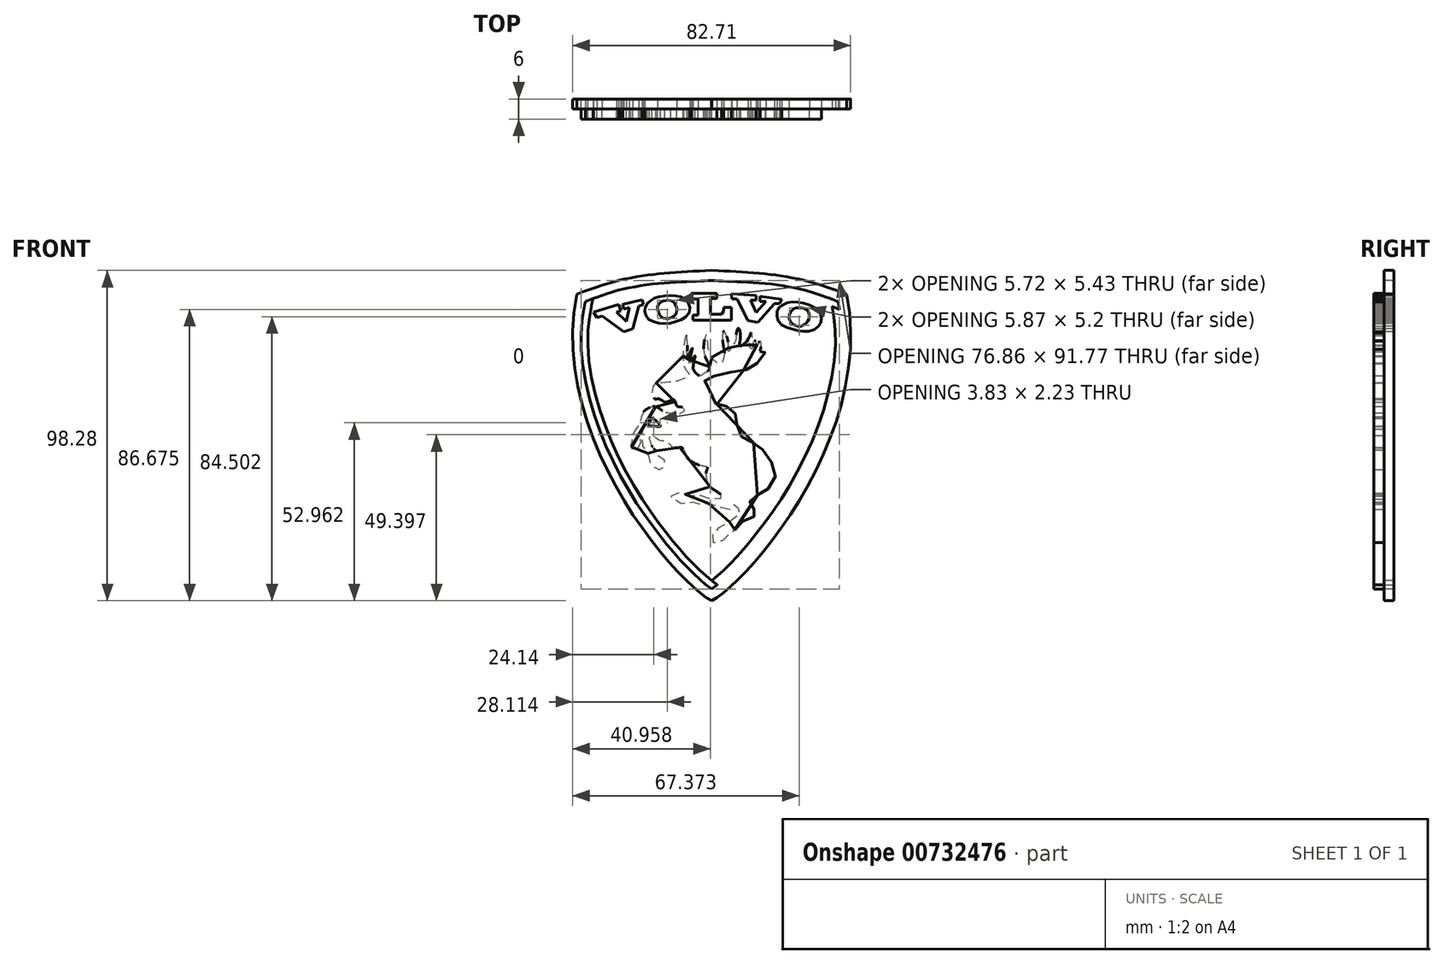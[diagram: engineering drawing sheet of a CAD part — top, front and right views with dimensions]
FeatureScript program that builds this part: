
annotation { "Feature Type Name" : "Feature", "Feature Type Description" : "" }
export const myFeature = defineFeature(function(context is Context, id is Id, definition is map)
    precondition{}
    {
        {
            var Q0;
            Q0=qCreatedBy(makeId("Front.planeOp"),FACE);
            var sketch = newSketch(context, id + "F0", { "sketchPlane" : qUnion([Q0])});
            skFitSpline(sketch, "E0", {"points": [v(28.32, -35.45) * mm, v(-11.84, 55.74) * mm], "startDerivative": vector(-32.94, 17.67) * mm, "endDerivative": vector(24.9, 126.93) * mm});
            skFitSpline(sketch, "E1", {"points": [v(-11.84, 55.74) * mm, v(28.32, 62.83) * mm], "startDerivative": vector(45.8, 18.48) * mm, "endDerivative": vector(43.78, 2) * mm});
            skFitSpline(sketch, "E2.MirrorCS", {"points": [v(68.5, 55.74) * mm, v(28.32, 62.83) * mm], "startDerivative": vector(-45.8, 18.48) * mm, "endDerivative": vector(-43.78, 2) * mm});
            skFitSpline(sketch, "E3.MirrorCS", {"points": [v(28.32, -35.45) * mm, v(68.5, 55.74) * mm], "startDerivative": vector(32.94, 17.67) * mm, "endDerivative": vector(-24.9, 126.93) * mm});
            skFitSpline(sketch, "E4.0", {"points": [v(29.74, -32.8) * mm, v(29.49, -32.67) * mm, v(28.89, -32.31) * mm, v(27.42, -31.29) * mm, v(25.17, -29.46) * mm, v(22.01, -26.47) * mm, v(18.52, -22.77) * mm, v(14.82, -18.42) * mm, v(9.76, -11.84) * mm, v(3.46, -2.28) * mm, v(-3.2, 10.82) * mm, v(-8.13, 25.08) * mm, v(-10.5, 40.02) * mm, v(-9.89, 50.13) * mm, v(-8.9, 55.16) * mm]});
            skFitSpline(sketch, "E4.1", {"points": [v(26.9, -32.8) * mm, v(27.16, -32.67) * mm, v(27.76, -32.31) * mm, v(29.23, -31.29) * mm, v(31.48, -29.46) * mm, v(34.64, -26.47) * mm, v(38.13, -22.77) * mm, v(41.83, -18.42) * mm, v(46.9, -11.84) * mm, v(53.2, -2.28) * mm, v(59.85, 10.82) * mm, v(64.78, 25.08) * mm, v(67.16, 40.02) * mm, v(66.54, 50.13) * mm, v(65.55, 55.16) * mm]});
            skFitSpline(sketch, "E4.2", {"points": [v(67.37, 52.95) * mm, v(63.66, 54.45) * mm, v(56.88, 56.72) * mm, v(47.72, 58.54) * mm, v(38.57, 59.38) * mm, v(31.84, 59.67) * mm, v(28.19, 59.84) * mm]});
            skFitSpline(sketch, "E4.3", {"points": [v(-10.72, 52.95) * mm, v(-7, 54.45) * mm, v(-0.23, 56.72) * mm, v(8.92, 58.54) * mm, v(18.08, 59.38) * mm, v(24.8, 59.67) * mm, v(28.46, 59.84) * mm]});
            skFitSpline(sketch, "E5.0", {"points": [v(30.69, -31.04) * mm, v(30.5, -30.94) * mm, v(29.99, -30.64) * mm, v(28.64, -29.7) * mm, v(26.5, -27.96) * mm, v(23.43, -25.06) * mm, v(20.01, -21.44) * mm, v(16.38, -17.17) * mm, v(11.4, -10.68) * mm, v(5.19, -1.27) * mm, v(-1.36, 11.61) * mm, v(-6.18, 25.59) * mm, v(-8.5, 40.13) * mm, v(-7.9, 49.91) * mm, v(-6.94, 54.77) * mm]});
            skFitSpline(sketch, "E5.1", {"points": [v(25.96, -31.04) * mm, v(26.15, -30.94) * mm, v(26.66, -30.64) * mm, v(28, -29.7) * mm, v(30.15, -27.96) * mm, v(33.22, -25.06) * mm, v(36.63, -21.44) * mm, v(40.27, -17.17) * mm, v(45.25, -10.68) * mm, v(51.46, -1.27) * mm, v(58, 11.61) * mm, v(62.83, 25.59) * mm, v(65.14, 40.13) * mm, v(64.54, 49.91) * mm, v(63.59, 54.77) * mm]});
            skFitSpline(sketch, "E5.2", {"points": [v(66.62, 51.1) * mm, v(62.98, 52.57) * mm, v(56.36, 54.78) * mm, v(47.45, 56.55) * mm, v(38.46, 57.39) * mm, v(31.76, 57.67) * mm, v(28.1, 57.84) * mm]});
            skFitSpline(sketch, "E5.3", {"points": [v(-9.97, 51.1) * mm, v(-6.33, 52.57) * mm, v(0.3, 54.78) * mm, v(9.2, 56.55) * mm, v(18.2, 57.39) * mm, v(24.9, 57.67) * mm, v(28.55, 57.84) * mm]});
            skLineSegment(sketch, "E6", {"start": v(-5.84, 48.83) * mm, "end": v(-4.27, 49.28) * mm});
            skLineSegment(sketch, "E7", {"start": v(-4.27, 49.28) * mm, "end": v(2.15, 44.6) * mm});
            skLineSegment(sketch, "E8", {"start": v(2.15, 44.6) * mm, "end": v(4.85, 45.45) * mm});
            skLineSegment(sketch, "E9", {"start": v(4.85, 45.45) * mm, "end": v(6.6, 52.26) * mm});
            skLineSegment(sketch, "E10", {"start": v(6.6, 52.26) * mm, "end": v(8.06, 52.71) * mm});
            skLineSegment(sketch, "E11", {"start": v(8.06, 52.71) * mm, "end": v(7.63, 54.12) * mm});
            skLineSegment(sketch, "E12", {"start": v(7.63, 54.12) * mm, "end": v(1.81, 52.71) * mm});
            skLineSegment(sketch, "E13", {"start": v(1.81, 52.71) * mm, "end": v(2.25, 51.3) * mm});
            skLineSegment(sketch, "E14", {"start": v(2.25, 51.3) * mm, "end": v(3.82, 51.79) * mm});
            skLineSegment(sketch, "E15", {"start": v(3.82, 51.79) * mm, "end": v(2.94, 47.7) * mm});
            skLineSegment(sketch, "E16", {"start": v(2.94, 47.7) * mm, "end": v(0, 50.4) * mm});
            skLineSegment(sketch, "E17", {"start": v(0, 50.4) * mm, "end": v(1.25, 50.79) * mm});
            skLineSegment(sketch, "E18", {"start": v(1.25, 50.79) * mm, "end": v(0.66, 52.71) * mm});
            skLineSegment(sketch, "E19", {"start": v(0.66, 52.71) * mm, "end": v(-6.84, 50.4) * mm});
            skLineSegment(sketch, "E20", {"start": v(-6.84, 50.4) * mm, "end": v(-5.84, 48.83) * mm});
            skFitSpline(sketch, "E21", {"points": [v(12.73, 49.84) * mm, v(13.92, 48.66) * mm, v(16.06, 48.66) * mm, v(17.3, 49.4) * mm, v(17.91, 50.52) * mm, v(17.86, 52.04) * mm, v(17.13, 53.33) * mm, v(15.83, 53.95) * mm, v(14.14, 53.78) * mm, v(12.57, 52.88) * mm, v(12.23, 51.3) * mm, v(12.73, 49.84) * mm]});
            skFitSpline(sketch, "E22", {"points": [v(8.46, 50.63) * mm, v(8.57, 51.87) * mm, v(9.53, 53.33) * mm, v(10.99, 54.4) * mm, v(12.9, 55.08) * mm, v(15.55, 55.36) * mm, v(17.86, 55.25) * mm, v(20, 54.63) * mm, v(21.46, 53.1) * mm, v(21.85, 50.85) * mm, v(20.4, 48.77) * mm, v(18.48, 47.81) * mm, v(15.66, 47.14) * mm, v(12.96, 47.08) * mm, v(10.31, 47.87) * mm, v(8.9, 49.1) * mm, v(8.46, 50.63) * mm]});
            skLineSegment(sketch, "E23", {"start": v(22.7, 49.56) * mm, "end": v(22.7, 48.04) * mm});
            skLineSegment(sketch, "E24", {"start": v(22.7, 48.04) * mm, "end": v(34.24, 48.04) * mm});
            skLineSegment(sketch, "E25", {"start": v(34.24, 48.04) * mm, "end": v(34.24, 51.87) * mm});
            skLineSegment(sketch, "E26", {"start": v(34.24, 51.87) * mm, "end": v(31.93, 51.87) * mm});
            skLineSegment(sketch, "E27", {"start": v(31.93, 51.87) * mm, "end": v(31.93, 50.85) * mm});
            skLineSegment(sketch, "E28", {"start": v(31.93, 50.85) * mm, "end": v(31.26, 49.84) * mm});
            skLineSegment(sketch, "E29", {"start": v(31.26, 49.84) * mm, "end": v(28, 49.84) * mm});
            skLineSegment(sketch, "E30", {"start": v(28, 49.84) * mm, "end": v(28, 54.51) * mm});
            skLineSegment(sketch, "E31", {"start": v(28, 54.51) * mm, "end": v(29.9, 54.51) * mm});
            skLineSegment(sketch, "E32", {"start": v(29.9, 54.51) * mm, "end": v(29.9, 56.03) * mm});
            skLineSegment(sketch, "E33", {"start": v(29.9, 56.03) * mm, "end": v(22.25, 56.03) * mm});
            skLineSegment(sketch, "E34", {"start": v(22.25, 56.03) * mm, "end": v(22.25, 54.4) * mm});
            skLineSegment(sketch, "E35", {"start": v(22.25, 54.4) * mm, "end": v(24.33, 54.4) * mm});
            skLineSegment(sketch, "E36", {"start": v(24.33, 54.4) * mm, "end": v(24.33, 49.56) * mm});
            skLineSegment(sketch, "E37", {"start": v(24.33, 49.56) * mm, "end": v(22.7, 49.56) * mm});
            skLineSegment(sketch, "E38", {"start": v(34.3, 54.35) * mm, "end": v(35.87, 54.35) * mm});
            skLineSegment(sketch, "E39", {"start": v(35.87, 54.35) * mm, "end": v(39.2, 47.87) * mm});
            skLineSegment(sketch, "E40", {"start": v(39.2, 47.87) * mm, "end": v(42, 47.42) * mm});
            skLineSegment(sketch, "E41", {"start": v(42, 47.42) * mm, "end": v(46.98, 52.94) * mm});
            skLineSegment(sketch, "E42", {"start": v(46.98, 52.94) * mm, "end": v(48.54, 52.94) * mm});
            skLineSegment(sketch, "E43", {"start": v(48.54, 52.94) * mm, "end": v(49.16, 54.29) * mm});
            skLineSegment(sketch, "E44", {"start": v(49.16, 54.29) * mm, "end": v(42.74, 55.15) * mm});
            skLineSegment(sketch, "E45", {"start": v(42.74, 55.15) * mm, "end": v(42.74, 53.67) * mm});
            skLineSegment(sketch, "E46", {"start": v(42.74, 53.67) * mm, "end": v(44.53, 53.67) * mm});
            skLineSegment(sketch, "E47", {"start": v(44.53, 53.67) * mm, "end": v(41.5, 50.35) * mm});
            skLineSegment(sketch, "E48", {"start": v(41.5, 50.35) * mm, "end": v(39.92, 54) * mm});
            skLineSegment(sketch, "E49", {"start": v(39.92, 54) * mm, "end": v(41.61, 54) * mm});
            skLineSegment(sketch, "E50", {"start": v(41.61, 54) * mm, "end": v(41.61, 55.36) * mm});
            skLineSegment(sketch, "E51", {"start": v(41.61, 55.36) * mm, "end": v(34.18, 55.92) * mm});
            skLineSegment(sketch, "E52", {"start": v(34.18, 55.92) * mm, "end": v(34.3, 54.35) * mm});
            skFitSpline(sketch, "E53", {"points": [v(51.75, 50.3) * mm, v(51.35, 48.88) * mm, v(51.75, 47.65) * mm, v(53.6, 46.35) * mm, v(55.91, 46.69) * mm, v(57.2, 48.2) * mm, v(57.38, 49.84) * mm, v(56.53, 51.25) * mm, v(54.67, 51.76) * mm, v(52.87, 51.47) * mm, v(51.75, 50.3) * mm]});
            skFitSpline(sketch, "E54", {"points": [v(47.8, 50.57) * mm, v(48.65, 52.04) * mm, v(51.18, 53.28) * mm, v(54.22, 53.39) * mm, v(57.55, 52.49) * mm, v(59.97, 50.97) * mm, v(60.92, 49.17) * mm, v(60.64, 47.03) * mm, v(59.12, 45.45) * mm, v(56.2, 44.66) * mm, v(53.6, 45.06) * mm, v(49.72, 46.35) * mm, v(48.03, 48.1) * mm, v(47.8, 50.57) * mm]});
            skSolve(sketch);
        }
        {
            var Q0;
            Q0=qCreatedBy(makeId("Front.planeOp"),FACE);
            var sketch = newSketch(context, id + "F1", { "sketchPlane" : qUnion([Q0])});
            skFitSpline(sketch, "E55", {"points": [v(35.17, -14.29) * mm, v(36.91, -12.28) * mm, v(39.59, -11.07) * mm, v(41.2, -10.07) * mm, v(41.26, -8.86) * mm, v(40.53, -7.8) * mm, v(39.66, -6.65) * mm, v(40.53, -4.58) * mm, v(42.6, -3.84) * mm, v(44.81, -2.44) * mm, v(47.15, 0.84) * mm, v(46.68, 4.8) * mm, v(44.07, 8.81) * mm, v(41.6, 11.15) * mm, v(38.92, 12.36) * mm, v(36.84, 13.83) * mm, v(35.77, 17.05) * mm, v(35.5, 19.46) * mm, v(34.63, 21.4) * mm, v(31.96, 22.54) * mm, v(29.61, 23.14) * mm, v(27.94, 26.49) * mm, v(26.73, 28.56) * mm, v(26.4, 30.57) * mm, v(28.68, 31.3) * mm, v(33.63, 32.44) * mm, v(38.72, 33.31) * mm, v(41.26, 34.79) * mm, v(43.47, 36.8) * mm, v(44.14, 39.34) * mm, v(42.73, 38.67) * mm, v(43.07, 40.48) * mm, v(42.6, 41.75) * mm, v(41.86, 40.61) * mm, v(41.33, 41.95) * mm, v(40.6, 41.08) * mm, v(40.66, 40) * mm, v(40.06, 39.54) * mm, v(39.66, 41.08) * mm, v(40.46, 42.62) * mm, v(40, 44.23) * mm, v(39.66, 43.22) * mm, v(37.38, 40.54) * mm, v(36.64, 40.54) * mm, v(36.91, 43.09) * mm, v(36.24, 45.63) * mm, v(35.7, 44.36) * mm, v(35.57, 42.49) * mm, v(34.7, 40.54) * mm, v(33.36, 38.74) * mm, v(33.23, 41.35) * mm, v(31.89, 44.7) * mm, v(31.55, 42.62) * mm, v(31.96, 39.67) * mm, v(32.1, 37.6) * mm, v(30.89, 35.06) * mm, v(28.4, 36.86) * mm, v(27.47, 38.94) * mm, v(27.07, 42.02) * mm, v(26.73, 43.76) * mm, v(26.2, 42.15) * mm, v(26, 39) * mm, v(26.73, 36.33) * mm, v(27.74, 33.85) * mm, v(26.94, 32.71) * mm, v(25.66, 31.9) * mm, v(24.66, 31.5) * mm, v(23.19, 32.85) * mm, v(22.78, 34.12) * mm, v(23.32, 37.47) * mm, v(21.78, 35.32) * mm, v(22.05, 37.4) * mm, v(22.52, 39.67) * mm, v(21.11, 37.26) * mm, v(21.04, 39.07) * mm, v(20.78, 43.42) * mm, v(20.04, 40.48) * mm, v(19.84, 37.6) * mm, v(20.24, 33.92) * mm, v(21.71, 31.57) * mm, v(19.5, 30.5) * mm, v(17.9, 29.83) * mm, v(15.89, 29.63) * mm, v(13.68, 29.36) * mm, v(11.87, 29.36) * mm, v(10.87, 28.16) * mm, v(10.67, 26.82) * mm, v(10.53, 25.88) * mm, v(11.14, 25.15) * mm, v(11.47, 24.48) * mm, v(12.4, 24.75) * mm, v(14.22, 23.74) * mm, v(16.22, 24.2) * mm, v(17.03, 24.34) * mm, v(17.56, 23.54) * mm, v(18.23, 22.33) * mm, v(19.64, 22.07) * mm, v(20.04, 20.93) * mm, v(19.04, 20.33) * mm, v(17.83, 19.32) * mm, v(15.76, 20.4) * mm, v(14.68, 20.46) * mm, v(12.07, 22.13) * mm, v(9.8, 22) * mm, v(7.65, 20.26) * mm, v(7.19, 18.18) * mm, v(6.11, 15.97) * mm, v(4.78, 14.03) * mm, v(4.57, 11.9) * mm, v(4.17, 10.95) * mm, v(4.57, 10.15) * mm, v(4.98, 9.41) * mm, v(7.25, 10.95) * mm, v(6.98, 12.9) * mm, v(7.65, 15.64) * mm, v(7.52, 11.9) * mm, v(8.12, 9.95) * mm, v(9.4, 8.4) * mm, v(9.73, 6.67) * mm, v(10.6, 4.93) * mm, v(12.2, 3.8) * mm, v(13.55, 3.72) * mm, v(14.42, 5.73) * mm, v(13.68, 7) * mm, v(11.8, 7.67) * mm, v(11.87, 9.01) * mm, v(10.93, 9.95) * mm, v(10.06, 12.16) * mm, v(9.8, 12.7) * mm, v(10.4, 13.77) * mm, v(12.88, 12.36) * mm, v(14.75, 12.1) * mm, v(16.63, 10.42) * mm, v(18.7, 10.15) * mm, v(19.44, 10.15) * mm, v(20.3, 8.81) * mm, v(21.04, 7.14) * mm, v(24.32, 5.06) * mm, v(27.07, 4.26) * mm, v(26.73, 2.99) * mm, v(27.27, -0.76) * mm, v(29.55, -2.77) * mm, v(31.82, -4.91) * mm, v(29.14, -5.18) * mm, v(26.73, -4.78) * mm, v(24.53, -4.1) * mm, v(22.32, -4.24) * mm, v(20.84, -3.77) * mm, v(19.24, -3.77) * mm, v(18.03, -3.37) * mm, v(16.16, -4.18) * mm, v(19.3, -6.52) * mm, v(23.05, -6.12) * mm, v(24.06, -6.65) * mm, v(25.73, -6.32) * mm, v(29.81, -7.19) * mm, v(32.76, -8.13) * mm, v(34.43, -8.06) * mm, v(34.97, -6.92) * mm, v(35.04, -6.45) * mm, v(36.64, -8.46) * mm, v(36.84, -9.4) * mm, v(33.76, -11.94) * mm, v(30.01, -14.08) * mm, v(28.74, -15.7) * mm, v(28.4, -17.97) * mm, v(30.68, -17.77) * mm, v(32.9, -16.7) * mm, v(33.56, -15.36) * mm, v(35.17, -14.29) * mm]});
            skFitSpline(sketch, "E56", {"points": [v(9.2, 16.58) * mm, v(9.93, 17.72) * mm, v(10.53, 18.79) * mm, v(13.08, 16.51) * mm, v(11, 16.58) * mm, v(9.2, 16.58) * mm]});
            skSolve(sketch);
        }
        {
            var Q0;
            Q0=makeQuery(id+"F0.imprint","IMPRINT",FACE,{"disambiguationData":[TD([[makeQuery(id+"F0.imprint","IMPRINT",EDGE,{"derivedFrom":sQuery(id+"F0.wireOp",EDGE,"E6")}),1.0]])]});
            var Q1;
            Q1=makeQuery(id+"F0.imprint","IMPRINT",FACE,{"disambiguationData":[TD([[makeQuery(id+"F0.imprint","IMPRINT",EDGE,{"derivedFrom":sQuery(id+"F0.wireOp",EDGE,"E21")}),-1.0]])]});
            var Q2;
            Q2=makeQuery(id+"F0.imprint","IMPRINT",FACE,{"disambiguationData":[TD([[makeQuery(id+"F0.imprint","IMPRINT",EDGE,{"derivedFrom":sQuery(id+"F0.wireOp",EDGE,"E23")}),1.0]])]});
            var Q3;
            Q3=makeQuery(id+"F0.imprint","IMPRINT",FACE,{"disambiguationData":[TD([[makeQuery(id+"F0.imprint","IMPRINT",EDGE,{"derivedFrom":sQuery(id+"F0.wireOp",EDGE,"E38")}),1.0]])]});
            var Q4;
            Q4=makeQuery(id+"F0.imprint","IMPRINT",FACE,{"disambiguationData":[TD([[makeQuery(id+"F0.imprint","IMPRINT",EDGE,{"derivedFrom":sQuery(id+"F0.wireOp",EDGE,"E53")}),-1.0]])]});
            extrude(context, id + "F2", {"entities" : qUnion([Q0, Q1, Q2, Q3, Q4]), "depth" : 3 * mm, "offsetDistance" : 25 * mm});
        }
        {
            var Q0;
            Q0=makeQuery(id+"F1.imprint","IMPRINT",FACE,{"disambiguationData":[TD([[makeQuery(id+"F1.imprint","IMPRINT",EDGE,{"derivedFrom":sQuery(id+"F1.wireOp",EDGE,"E55")}),1.0]])]});
            extrude(context, id + "F3", {"entities" : qUnion([Q0]), "depth" : 3 * mm, "offsetDistance" : 25 * mm});
        }
        {
            var Q0;
            Q0=makeQuery(id+"F0.imprint","IMPRINT",FACE,{"disambiguationData":[TD([[makeQuery(id+"F0.imprint","IMPRINT",EDGE,{"derivedFrom":sQuery(id+"F0.wireOp",EDGE,"E4.0")}),-1.0]])]});
            extrude(context, id + "F4", {"entities" : qUnion([Q0]), "depth" : 3 * mm, "offsetDistance" : 25 * mm});
        }
        {
            var Q0;
            Q0=makeQuery(id+"F0.imprint","IMPRINT",FACE,{"disambiguationData":[TD([[makeQuery(id+"F0.imprint","IMPRINT",EDGE,{"derivedFrom":sQuery(id+"F0.wireOp",EDGE,"E0")}),-1.0]])]});
            var Q1;
            {var subQ4=sQuery(id+"F0.wireOp",EDGE,"E5.2");Q1=makeQuery(id+"F0.imprint","IMPRINT",FACE,{"disambiguationData":[TD([[makeQuery(id+"F0.imprint","IMPRINT",EDGE,{"derivedFrom":subQ4}),1.0]])]});}
            extrude(context, id + "F5", {"entities" : qUnion([Q0, Q1]), "operationType" : NewBodyOperationType.ADD, "oppositeDirection" : true, "depth" : 3 * mm, "offsetDistance" : 25 * mm});
        }
        {
            var Q0;
            Q0=makeQuery(id+"F0.imprint","IMPRINT",FACE,{"disambiguationData":[TD([[makeQuery(id+"F0.imprint","IMPRINT",EDGE,{"derivedFrom":sQuery(id+"F0.wireOp",EDGE,"E4.0")}),-1.0]])]});
            extrude(context, id + "F6", {"entities" : qUnion([Q0]), "oppositeDirection" : true, "depth" : 3 * mm, "offsetDistance" : 25 * mm});
        }
        {
            var Q0;
            Q0=makeQuery(id+"F2.opExtrude","CAP_FACE",FACE,{"disambiguationData":[OSD([sQuery(id+"F0.wireOp",EDGE,"E38"),sQuery(id+"F0.wireOp",EDGE,"E39"),sQuery(id+"F0.wireOp",EDGE,"E40"),sQuery(id+"F0.wireOp",EDGE,"E41"),sQuery(id+"F0.wireOp",EDGE,"E42"),sQuery(id+"F0.wireOp",EDGE,"E43"),sQuery(id+"F0.wireOp",EDGE,"E44"),sQuery(id+"F0.wireOp",EDGE,"E45"),sQuery(id+"F0.wireOp",EDGE,"E46"),sQuery(id+"F0.wireOp",EDGE,"E47"),sQuery(id+"F0.wireOp",EDGE,"E48"),sQuery(id+"F0.wireOp",EDGE,"E49"),sQuery(id+"F0.wireOp",EDGE,"E50"),sQuery(id+"F0.wireOp",EDGE,"E51"),sQuery(id+"F0.wireOp",EDGE,"E52")])],"isStart":true});
            var Q1;
            Q1=makeQuery(id+"F2.opExtrude","CAP_FACE",FACE,{"disambiguationData":[OSD([sQuery(id+"F0.wireOp",EDGE,"E23"),sQuery(id+"F0.wireOp",EDGE,"E24"),sQuery(id+"F0.wireOp",EDGE,"E25"),sQuery(id+"F0.wireOp",EDGE,"E26"),sQuery(id+"F0.wireOp",EDGE,"E27"),sQuery(id+"F0.wireOp",EDGE,"E28"),sQuery(id+"F0.wireOp",EDGE,"E29"),sQuery(id+"F0.wireOp",EDGE,"E30"),sQuery(id+"F0.wireOp",EDGE,"E31"),sQuery(id+"F0.wireOp",EDGE,"E32"),sQuery(id+"F0.wireOp",EDGE,"E33"),sQuery(id+"F0.wireOp",EDGE,"E34"),sQuery(id+"F0.wireOp",EDGE,"E35"),sQuery(id+"F0.wireOp",EDGE,"E36"),sQuery(id+"F0.wireOp",EDGE,"E37")])],"isStart":true});
            var Q2;
            Q2=makeQuery(id+"F2.opExtrude","CAP_FACE",FACE,{"disambiguationData":[OSD([sQuery(id+"F0.wireOp",EDGE,"E21"),sQuery(id+"F0.wireOp",EDGE,"E22")])],"isStart":true});
            var Q3;
            Q3=makeQuery(id+"F2.opExtrude","CAP_FACE",FACE,{"disambiguationData":[OSD([sQuery(id+"F0.wireOp",EDGE,"E6"),sQuery(id+"F0.wireOp",EDGE,"E7"),sQuery(id+"F0.wireOp",EDGE,"E8"),sQuery(id+"F0.wireOp",EDGE,"E9"),sQuery(id+"F0.wireOp",EDGE,"E10"),sQuery(id+"F0.wireOp",EDGE,"E11"),sQuery(id+"F0.wireOp",EDGE,"E12"),sQuery(id+"F0.wireOp",EDGE,"E13"),sQuery(id+"F0.wireOp",EDGE,"E14"),sQuery(id+"F0.wireOp",EDGE,"E15"),sQuery(id+"F0.wireOp",EDGE,"E16"),sQuery(id+"F0.wireOp",EDGE,"E17"),sQuery(id+"F0.wireOp",EDGE,"E18"),sQuery(id+"F0.wireOp",EDGE,"E19"),sQuery(id+"F0.wireOp",EDGE,"E20")])],"isStart":true});
            var Q4;
            Q4=makeQuery(id+"F2.opExtrude","CAP_FACE",FACE,{"disambiguationData":[OSD([sQuery(id+"F0.wireOp",EDGE,"E53"),sQuery(id+"F0.wireOp",EDGE,"E54")])],"isStart":true});
            extrude(context, id + "F7", {"entities" : qUnion([Q0, Q1, Q2, Q3, Q4]), "depth" : 3 * mm, "offsetDistance" : 25 * mm});
        }
    });
